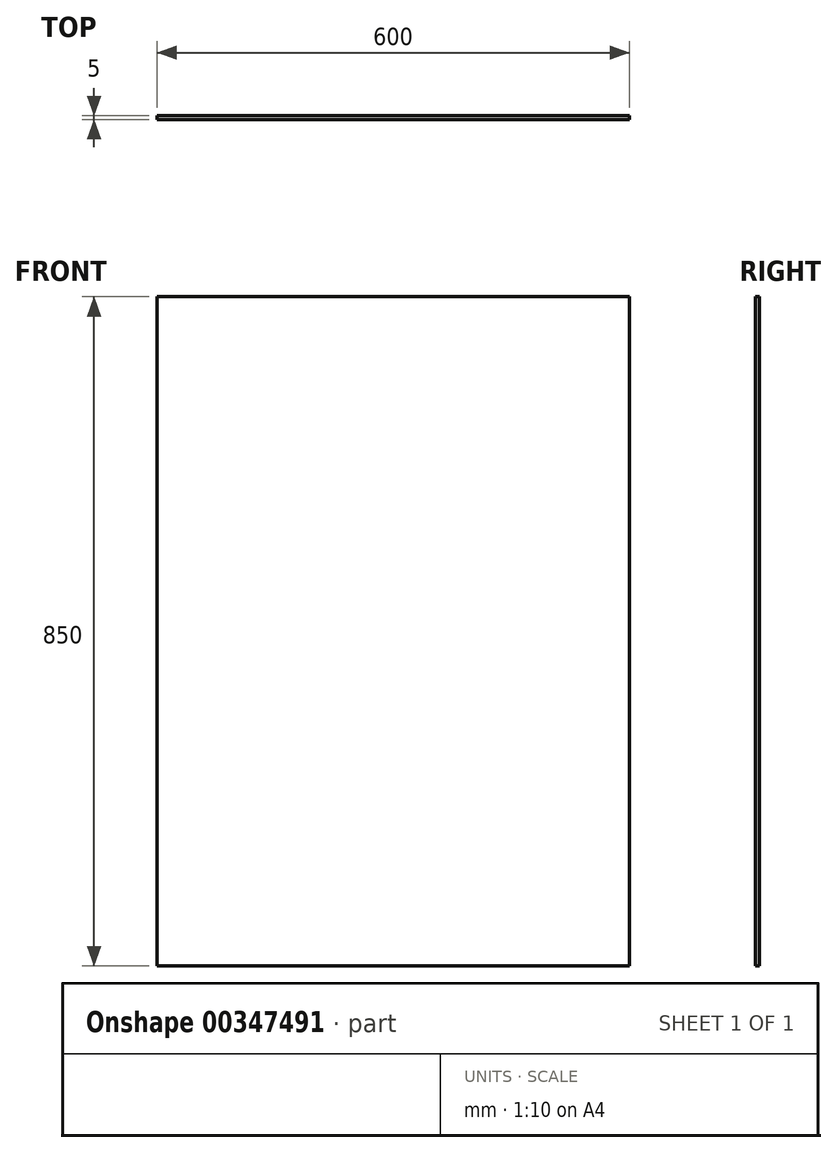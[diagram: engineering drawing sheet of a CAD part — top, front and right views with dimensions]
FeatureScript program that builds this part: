
annotation { "Feature Type Name" : "Feature", "Feature Type Description" : "" }
export const myFeature = defineFeature(function(context is Context, id is Id, definition is map)
    precondition{}
    {
        {
            var Q0;
            Q0=qCreatedBy(makeId("Front.planeOp"),FACE);
            var sketch = newSketch(context, id + "F0", { "sketchPlane" : qUnion([Q0])});
            skLineSegment(sketch, "E0.bottom", {"start": v(-39.41, 785.08) * mm, "end": v(560.59, 785.08) * mm});
            skLineSegment(sketch, "E0.top", {"start": v(-39.41, -64.92) * mm, "end": v(560.59, -64.92) * mm});
            skLineSegment(sketch, "E0.left", {"start": v(-39.41, 785.08) * mm, "end": v(-39.41, -64.92) * mm});
            skLineSegment(sketch, "E0.right", {"start": v(560.59, 785.08) * mm, "end": v(560.59, -64.92) * mm});
            skLineSegment(sketch, "E1.0", {"start": v(-24.41, 770.08) * mm, "end": v(545.59, 770.08) * mm});
            skLineSegment(sketch, "E1.1", {"start": v(-24.41, 770.08) * mm, "end": v(-24.41, -49.92) * mm});
            skLineSegment(sketch, "E1.2", {"start": v(-24.41, -49.92) * mm, "end": v(545.59, -49.92) * mm});
            skLineSegment(sketch, "E1.3", {"start": v(545.59, 770.08) * mm, "end": v(545.59, -49.92) * mm});
            skSolve(sketch);
        }
        {
            var Q0;
            Q0=qSketchRegion(id+"F0",true);
            extrude(context, id + "F1", {"entities" : qUnion([Q0]), "depth" : 20 * mm});
        }
        {
            var Q0;
            Q0=makeQuery(id+"F1.opExtrude","CAP_FACE",FACE,{"disambiguationData":[OSD([sQuery(id+"F0.wireOp",EDGE,"E0.bottom"),sQuery(id+"F0.wireOp",EDGE,"E0.top"),sQuery(id+"F0.wireOp",EDGE,"E0.left"),sQuery(id+"F0.wireOp",EDGE,"E0.right"),sQuery(id+"F0.wireOp",EDGE,"E1.0"),sQuery(id+"F0.wireOp",EDGE,"E1.1"),sQuery(id+"F0.wireOp",EDGE,"E1.2"),sQuery(id+"F0.wireOp",EDGE,"E1.3")])],"isStart":false});
            var sketch = newSketch(context, id + "F2", { "sketchPlane" : qUnion([Q0])});
            skLineSegment(sketch, "E2.bottom", {"start": v(-39.41, 785.08) * mm, "end": v(560.59, 785.08) * mm});
            skLineSegment(sketch, "E2.top", {"start": v(-39.41, -64.92) * mm, "end": v(560.59, -64.92) * mm});
            skLineSegment(sketch, "E2.left", {"start": v(-39.41, 785.08) * mm, "end": v(-39.41, -64.92) * mm});
            skLineSegment(sketch, "E2.right", {"start": v(560.59, 785.08) * mm, "end": v(560.59, -64.92) * mm});
            skSolve(sketch);
        }
        {
            var Q0;
            Q0=qSketchRegion(id+"F2",true);
            extrude(context, id + "F3", {"entities" : qUnion([Q0]), "operationType" : NewBodyOperationType.ADD, "oppositeDirection" : true, "depth" : 5 * mm});
        }
        {
            var Q0;
            Q0=makeQuery(id+"F1.opExtrude","CAP_FACE",FACE,{"disambiguationData":[OSD([sQuery(id+"F0.wireOp",EDGE,"E0.bottom"),sQuery(id+"F0.wireOp",EDGE,"E0.top"),sQuery(id+"F0.wireOp",EDGE,"E0.left"),sQuery(id+"F0.wireOp",EDGE,"E0.right"),sQuery(id+"F0.wireOp",EDGE,"E1.0"),sQuery(id+"F0.wireOp",EDGE,"E1.1"),sQuery(id+"F0.wireOp",EDGE,"E1.2"),sQuery(id+"F0.wireOp",EDGE,"E1.3")])],"isStart":true});
            var sketch = newSketch(context, id + "F4", { "sketchPlane" : qUnion([Q0])});
            skLineSegment(sketch, "E3.bottom", {"start": v(-560.59, 785.08) * mm, "end": v(39.41, 785.08) * mm});
            skLineSegment(sketch, "E3.top", {"start": v(-560.59, -64.92) * mm, "end": v(39.41, -64.92) * mm});
            skLineSegment(sketch, "E3.left", {"start": v(-560.59, 785.08) * mm, "end": v(-560.59, -64.92) * mm});
            skLineSegment(sketch, "E3.right", {"start": v(39.41, 785.08) * mm, "end": v(39.41, -64.92) * mm});
            skSolve(sketch);
        }
        {
            var Q0;
            Q0=qSketchRegion(id+"F4",true);
            var Q1;
            Q1=makeQuery(id+"F3.opExtrude","CAP_FACE",FACE,{"disambiguationData":[OSD([sQuery(id+"F2.wireOp",EDGE,"E2.bottom"),sQuery(id+"F2.wireOp",EDGE,"E2.top"),sQuery(id+"F2.wireOp",EDGE,"E2.left"),sQuery(id+"F2.wireOp",EDGE,"E2.right")])],"isStart":false});
            extrude(context, id + "F5", {"entities" : qUnion([Q0]), "operationType" : NewBodyOperationType.REMOVE, "endBound" : BoundingType.UP_TO_SURFACE, "oppositeDirection" : true, "endBoundEntityFace" : qUnion([Q1]), "depth" : 25 * mm});
        }
    });
